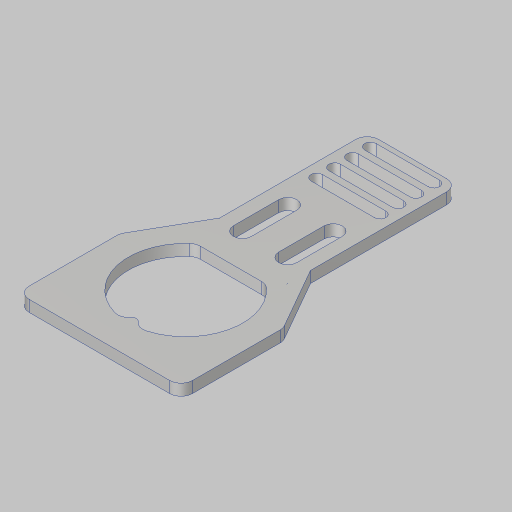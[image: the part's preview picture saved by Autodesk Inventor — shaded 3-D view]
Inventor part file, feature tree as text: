
AUTODESK INVENTOR PART (.ipt)
format: ipt  version: 2023.5 (Build 275446000, 446)  size: 263,680 bytes
history: native  units: in
note: dims shown in document units (in); Inventor stores cm internally (conversion verified against a paired STEP export)
features: sketch x5, extrude x5, fillet x4, projected_geometry x4
ambient origin geometry x8: Origin, YZ Plane, XZ Plane, XY Plane, X Axis, Y Axis, Z Axis, Center Point
bodies: Solid1 (feature_tree)
feature tree (18):
  sketch  "Sketch1"  dims[d1=0.7in d3=0.125in d4=0.197in]
  extrude  "Extrusion1"  Depth=0.125in
  fillet  "Fillet1"  Radius=0.197in
  extrude  "Extrusion2"  Depth=1.0in
  extrude  "Extrusion3"  Depth=0.25in
  fillet  "Fillet2"  Radius=0.5in
  extrude  "Extrusion4"  Depth=0.125in TaperAngle=0.0deg
  fillet  "Fillet3"  Radius=0.125in
  extrude  "Extrusion5"  Depth=0.5in
  fillet  "Fillet4"  Radius=1.375in
  sketch  "Sketch2"  dims[d5=0.197in d8=1.0in]
  sketch  "Sketch3"  dims[d9=2.0in d10=0.25in d11=0.5in]
  sketch  "Sketch4"  dims[d12=0.25in d13=0.125in d14=0.0in d22=0.125in]
  sketch  "Sketch5"  dims[d23=0.201in d24=0.5in d26=1.375in d27=0.5in d28=1.0in d29=0.0in d30=1.26in d31=0.5in d32=0.125in d33=1.0in d34=0.0in d35=0.125in d36=0.093in d37=0.042in d38=1.0in d39=0.0in d40=0.125in d41=0.7874in d43=0.197in d44=0.3937in d46=1.0in d48=1.8in d49=3.45in d50=1.125in d51=1.0in d52=0.0in d53=0.125in]
  projected_geometry  "Project Cut Edges1"
  projected_geometry  "Project Cut Edges2"
  projected_geometry  "Project Cut Edges3"
  projected_geometry  "Project Cut Edges4"
